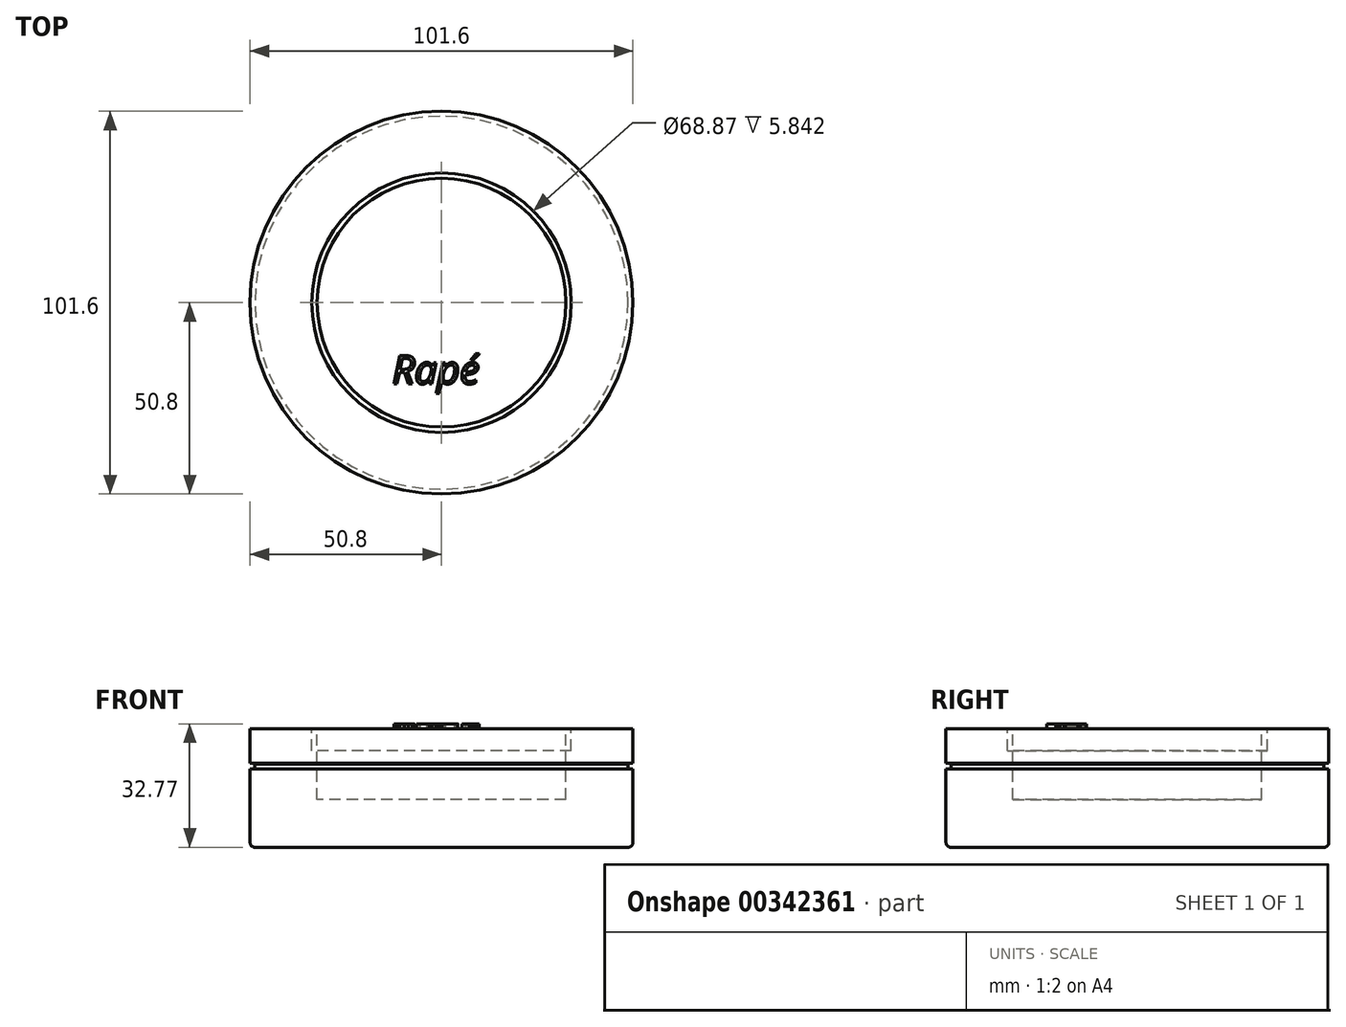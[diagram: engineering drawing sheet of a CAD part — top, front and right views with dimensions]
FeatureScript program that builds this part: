
annotation { "Feature Type Name" : "Feature", "Feature Type Description" : "" }
export const myFeature = defineFeature(function(context is Context, id is Id, definition is map)
    precondition{}
    {
        {
            var Q0;
            Q0=qCreatedBy(makeId("Top.planeOp"),FACE);
            var sketch = newSketch(context, id + "F0", { "sketchPlane" : qUnion([Q0])});
            skCircle(sketch, "E0", {"center": v(0, 0) * mm, "radius": 50.8 * mm});
            skSolve(sketch);
        }
        {
            var Q0;
            Q0=makeQuery(id+"F0.imprint","IMPRINT",FACE,{"disambiguationData":[TD([[makeQuery(id+"F0.imprint","IMPRINT",EDGE,{"derivedFrom":sQuery(id+"F0.wireOp",EDGE,"E0")}),1.0]])]});
            extrude(context, id + "F1", {"entities" : qUnion([Q0]), "depth" : 20.83 * mm});
        }
        {
            var Q0;
            Q0=qCreatedBy(makeId("Top.planeOp"),FACE);
            cPlane(context, id + "F2", {"entities" : qUnion([Q0]), "cplaneType" : CPlaneType.OFFSET, "offset" : 21.08 * mm, "width" : 152.4 * mm, "height" : 152.4 * mm});
        }
        {
            var Q0;
            Q0=makeQuery(id+"F1.opExtrude","CAP_FACE",FACE,{"disambiguationData":[OSD([sQuery(id+"F0.wireOp",EDGE,"E0")])],"isStart":false});
            var sketch = newSketch(context, id + "F3", { "sketchPlane" : qUnion([Q0])});
            skCircle(sketch, "E1", {"center": v(0, 0) * mm, "radius": 49.5 * mm});
            skSolve(sketch);
        }
        {
            var Q0;
            Q0=makeQuery(id+"F3.imprint","IMPRINT",FACE,{"disambiguationData":[TD([[makeQuery(id+"F3.imprint","IMPRINT",EDGE,{"derivedFrom":sQuery(id+"F3.wireOp",EDGE,"E1")}),1.0]])]});
            extrude(context, id + "F4", {"entities" : qUnion([Q0]), "operationType" : NewBodyOperationType.ADD, "depth" : 1.27 * mm});
        }
        {
            var Q0;
            Q0=qCreatedBy(id+"F2.planeOp",FACE);
            cPlane(context, id + "F5", {"entities" : qUnion([Q0]), "cplaneType" : CPlaneType.OFFSET, "offset" : 1.27 * mm, "width" : 152.4 * mm, "height" : 152.4 * mm});
        }
        {
            var Q0;
            Q0=qCreatedBy(id+"F5.planeOp",FACE);
            var sketch = newSketch(context, id + "F6", { "sketchPlane" : qUnion([Q0])});
            skCircle(sketch, "E2", {"center": v(0, 0) * mm, "radius": 50.8 * mm});
            skSolve(sketch);
        }
        {
            var Q0;
            Q0=makeQuery(id+"F6.imprint","IMPRINT",FACE,{"disambiguationData":[TD([[makeQuery(id+"F6.imprint","IMPRINT",EDGE,{"derivedFrom":sQuery(id+"F6.wireOp",EDGE,"E2")}),1.0]])]});
            extrude(context, id + "F7", {"entities" : qUnion([Q0]), "depth" : 9.14 * mm});
        }
        {
            var Q0;
            Q0=makeQuery(id+"F7.opExtrude","CAP_FACE",FACE,{"disambiguationData":[OSD([sQuery(id+"F6.wireOp",EDGE,"E2")])],"isStart":false});
            var sketch = newSketch(context, id + "F8", { "sketchPlane" : qUnion([Q0])});
            skCircle(sketch, "E3", {"center": v(0, 0) * mm, "radius": 34.43 * mm});
            skSolve(sketch);
        }
        {
            var Q0;
            Q0=makeQuery(id+"F8.imprint","IMPRINT",FACE,{"disambiguationData":[TD([[makeQuery(id+"F8.imprint","IMPRINT",EDGE,{"derivedFrom":sQuery(id+"F8.wireOp",EDGE,"E3")}),1.0]])]});
            var sketch = newSketch(context, id + "F9", { "sketchPlane" : qUnion([Q0])});
            skCircle(sketch, "E4", {"center": v(0, 0) * mm, "radius": 33.02 * mm});
            skSolve(sketch);
        }
        {
            var Q0;
            Q0=makeQuery(id+"F8.imprint","IMPRINT",FACE,{"disambiguationData":[TD([[makeQuery(id+"F8.imprint","IMPRINT",EDGE,{"derivedFrom":sQuery(id+"F8.wireOp",EDGE,"E3")}),1.0]])]});
            extrude(context, id + "F10", {"entities" : qUnion([Q0]), "operationType" : NewBodyOperationType.REMOVE, "oppositeDirection" : true, "depth" : 5.84 * mm});
        }
        {
            var Q0;
            Q0=makeQuery(id+"F9.imprint","IMPRINT",FACE,{"disambiguationData":[TD([[makeQuery(id+"F9.imprint","IMPRINT",EDGE,{"derivedFrom":sQuery(id+"F9.wireOp",EDGE,"E4")}),1.0]])]});
            extrude(context, id + "F11", {"entities" : qUnion([Q0]), "oppositeDirection" : true, "depth" : 18.8 * mm});
        }
        {
            var Q0;
            Q0=qCreatedBy(makeId("Top.planeOp"),FACE);
            cPlane(context, id + "F12", {"entities" : qUnion([Q0]), "cplaneType" : CPlaneType.OFFSET, "offset" : 31.5 * mm, "width" : 152.4 * mm, "height" : 152.4 * mm});
        }
        {
            var Q0;
            Q0=qCreatedBy(id+"F12.planeOp",FACE);
            var sketch = newSketch(context, id + "F13", { "sketchPlane" : qUnion([Q0])});
            skText(sketch, "E5", { "text": "XR", "fontName": "OpenSans-Regular.ttf"});
            const initialGuessF13  = {"E5": [-0.0189, -0.01045, 1, 0, 0.02022]};
            skSetInitialGuess(sketch, initialGuessF13);
            skSolve(sketch);
        }
        {
            var Q0;
            Q0 = qConstructionFilter(qBodyType(qCreatedBy(id + "F13" ,EDGE), BodyType.WIRE), ConstructionObject.NO);
            extrude(context, id + "F14", {"bodyType" : ToolBodyType.SURFACE, "surfaceEntities" : qUnion([Q0]), "depth" : 1.27 * mm});
        }
        {
            var Q0;
            Q0=qCreatedBy(id+"F12.planeOp",FACE);
            var sketch = newSketch(context, id + "F15", { "sketchPlane" : qUnion([Q0])});
            skText(sketch, "E6", { "text": "Göteborgs", "fontName": "OpenSans-Italic.ttf"});
            const initialGuessF15  = {"E6": [-0.02134, 0.01334, 1, 0, 0.00645]};
            skSetInitialGuess(sketch, initialGuessF15);
            skSolve(sketch);
        }
        {
            var Q0;
            Q0 = qConstructionFilter(qBodyType(qCreatedBy(id + "F15" ,EDGE), BodyType.WIRE), ConstructionObject.NO);
            extrude(context, id + "F16", {"bodyType" : ToolBodyType.SURFACE, "surfaceEntities" : qUnion([Q0]), "depth" : 1.27 * mm});
        }
        {
            var Q0;
            Q0=qCreatedBy(id+"F12.planeOp",FACE);
            var sketch = newSketch(context, id + "F17", { "sketchPlane" : qUnion([Q0])});
            skText(sketch, "E7", { "text": "Rapé", "fontName": "OpenSans-Italic.ttf"});
            const initialGuessF17  = {"E7": [-0.01311, -0.02156, 1, 0, 0.00756]};
            skSetInitialGuess(sketch, initialGuessF17);
            skSolve(sketch);
        }
        {
            var Q0;
            Q0 = qSketchRegion(id + "F17", true);
            extrude(context, id + "F18", {"entities" : qUnion([Q0]), "operationType" : NewBodyOperationType.ADD, "depth" : 1.27 * mm});
        }
        {
            var Q0;
            Q0=makeQuery(id+"F1.opExtrude","CAP_EDGE",EDGE,{"disambiguationData":[OSD([sQuery(id+"F0.wireOp",EDGE,"E0")])],"isStart":true});
            fillet(context, id + "F19", {"entities" : qUnion([Q0]), "radius" : 1.27 * mm, "tangentPropagation" : true, "allowEdgeOverflow" : false});
        }
    });
